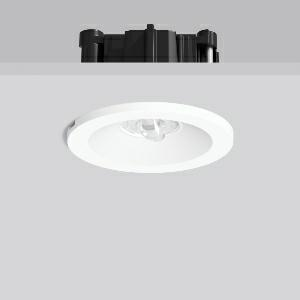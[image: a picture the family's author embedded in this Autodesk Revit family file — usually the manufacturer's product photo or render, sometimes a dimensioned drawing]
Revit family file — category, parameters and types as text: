
# Revit family: turia_l_672561_002_c7d4
name_source: partatom
category: Lighting Fixtures
units: mm (PartAtom-declared; Revit-internal decimal feet)

## family parameters
Cut with Voids When Loaded = No
Host = Face
Light Source = No
Part Type = Normal
Room Calculation Point = No
Round Connector Dimension = Use Diameter
Shared = No

## types (1)
- TURIA L (1 x LED Modul 765, 270 lm, 6500)
    Apparent Load = 4 VA
    CIE Flux Codes = 70 91 99 100 100
    Color Rendering = 70
    Color Temperature = 6500
    Default Elevation = 1800 mm
    Description = Series: TURIA L
Round emergency luminaire for escape route lighting. Housing: die-cast aluminium. Bezel ring: plastic. With asymmetrical beam plastic lenses for illuminating rescue facilities. Einzelbatteriesystem mit automatischem Selbsttest. With enclosed separate ceiling mounting ring also suitable for ceiling cut-outs of Ø 68 mm. 
Colour: white
Diameter: 62 mm
Height: 3 mm
Cut-out diameter: 54-68 mm
Recess height: 76-162 mm
Luminaire: recess height: 42 mm
Weight: 420 g
Operating mode: non-maintained power mode
Duration time: 3 h
Lamp: LED
Socket: without socket
Colour temperature: 6500K
Colour rendering index (CRI): 70
System power: 4.2 W
Rated luminous flux: 270 lm
Luminous flux, emergency: 190 lm
System power, emergency: -
Control gear: Regulated power supply
Protection class: II
Type of protection: IP 20
    Height = 0 mm  [stored 0 ft]
    Lamp = 1 x LED Modul 765
    Lamp Light Flux = 270 lm
    Lamp count = 1
    Length = 62 mm  [stored 0.203412 ft]
    Lifetime = 50000 h
    Luminous efficacy = 64 lm/W
    Manufacturer = RZB
    ModVariant = No
    Model = 672561.002
    Mounting Place = Ceiling
    Mounting Type = Recessed
    Number of Poles = 1
    OnlyDefault = Yes
    Power Factor = 1
    Product Name = TURIA L
    Product group = Recessed ceiling luminaires
    ProductGroupID = 405
    Protection Class = Protection class II
    Protection Degree = IP 20
    RLX_Detail_Level = 1
    RLX_Emergency_Light_Flux = 190 lm
    RLX_Emergency_Type = 3
    RLX_Emergency_Type_DB = Yes
    RlxData = <blob elided: 55217 chars, md5=20883917>
    Socket = socket
    Standby Power = 0 W
    System Light Flux = 270 lm
    System Power = 4 W
    Type Comments = Product without accessories
    Type Image = 672561.002.jpg
    URL = http://relux.com
    VarID = ---
    Voltage = 230 V
    Voltage Range = 220-240 V
    Weight = 0.00 kg
    Width = 0 mm  [stored 0 ft]

note: [stored X ft] marks values corroborated as IEEE doubles in the binary element streams (Revit-internal decimal feet)

## geometry (parser evidence)
native form markers: Blend x4, Sweep x10
no freeform markers — native parametric forms only
